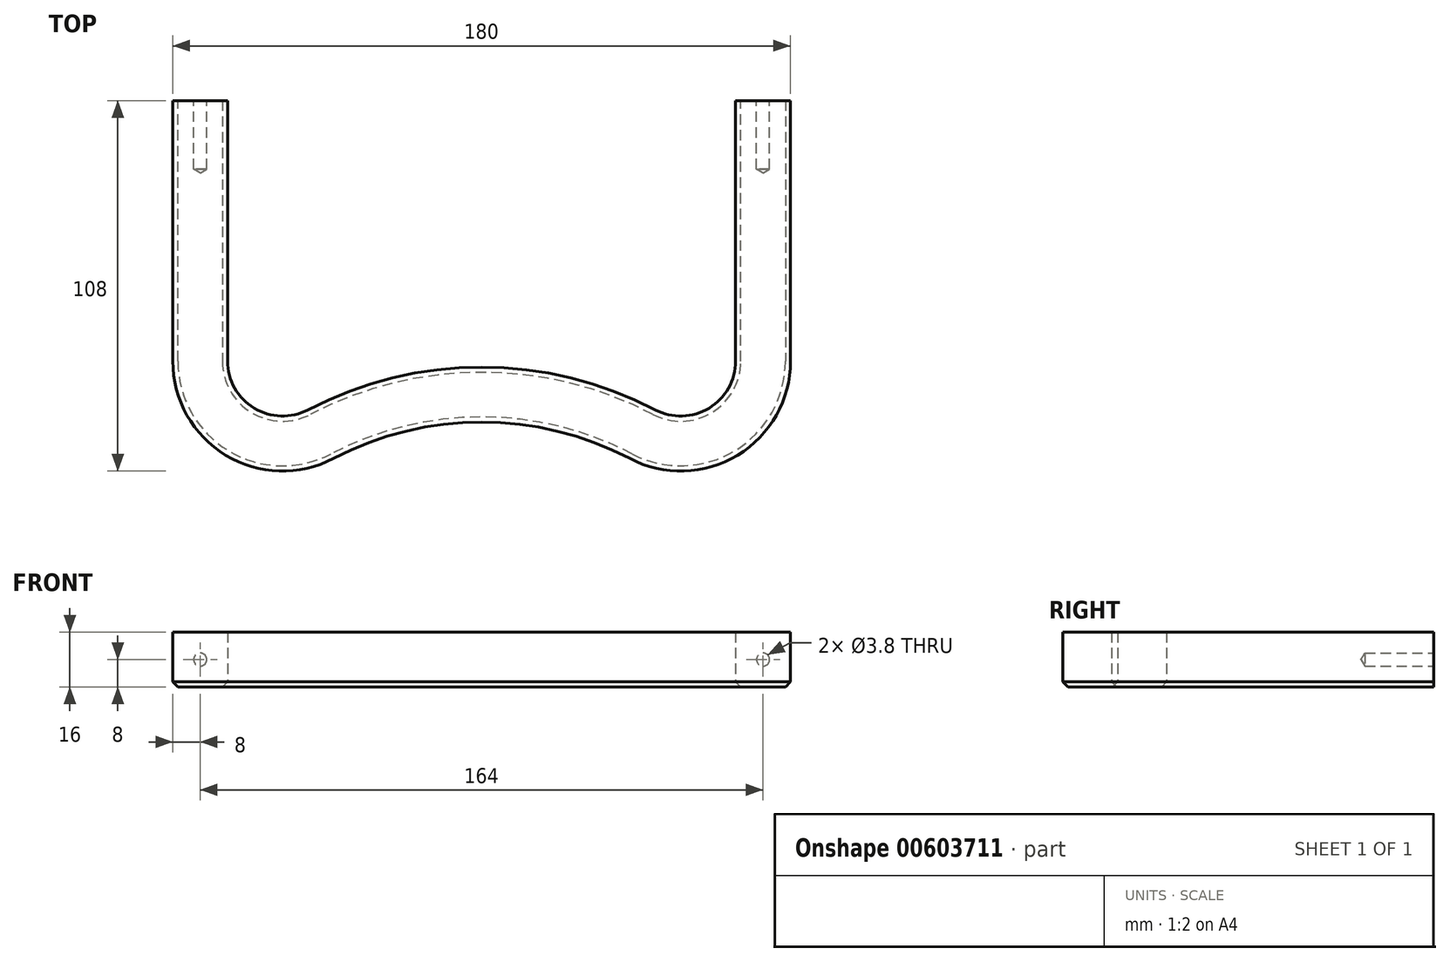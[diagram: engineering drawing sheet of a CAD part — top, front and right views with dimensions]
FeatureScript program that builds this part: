
annotation { "Feature Type Name" : "Feature", "Feature Type Description" : "" }
export const myFeature = defineFeature(function(context is Context, id is Id, definition is map)
    precondition{}
    {
        {
            var Q0;
            Q0=qCreatedBy(makeId("Top.planeOp"),FACE);
            var sketch = newSketch(context, id + "F0", { "sketchPlane" : qUnion([Q0])});
            skLineSegment(sketch, "E0", {"start": v(0, 84.42) * mm, "end": v(0, -84.76) * mm, "construction": true});
            skLineSegment(sketch, "E1.right", {"start": v(-74, 61.2) * mm, "end": v(-74, -14.8) * mm});
            skPoint(sketch, "E1.middle", {"position": v(0, 0) * mm});
            skArc(sketch, "E2", {"start": v(-74, -14.8) * mm, "mid": v(-66.29, -28.49) * mm, "end": v(-50.58, -28.98) * mm});
            skPoint(sketch, "E3.orphan", {"position": v(-74, -33.07) * mm});
            skArc(sketch, "E4", {"start": v(0, -16.55) * mm, "mid": v(-26.04, -19.7) * mm, "end": v(-50.58, -28.98) * mm});
            skArc(sketch, "E5.0", {"start": v(0, -32.55) * mm, "mid": v(-22.23, -35.24) * mm, "end": v(-43.17, -43.15) * mm});
            skArc(sketch, "E5.1", {"start": v(-90, -14.8) * mm, "mid": v(-74.57, -42.17) * mm, "end": v(-43.17, -43.15) * mm});
            skLineSegment(sketch, "E5.2", {"start": v(-90, 61.2) * mm, "end": v(-90, -14.8) * mm});
            skLineSegment(sketch, "E6", {"start": v(-90, 61.2) * mm, "end": v(-74, 61.2) * mm});
            skLineSegment(sketch, "E7.MirrorCS", {"start": v(90, 61.2) * mm, "end": v(74, 61.2) * mm});
            skLineSegment(sketch, "E8.MirrorCS", {"start": v(90, 61.2) * mm, "end": v(90, -14.8) * mm});
            skLineSegment(sketch, "E9.MirrorCS", {"start": v(74, 61.2) * mm, "end": v(74, -14.8) * mm});
            skArc(sketch, "E10.MirrorCS", {"start": v(90, -14.8) * mm, "mid": v(74.57, -42.17) * mm, "end": v(43.17, -43.15) * mm});
            skArc(sketch, "E11.MirrorCS", {"start": v(74, -14.8) * mm, "mid": v(66.29, -28.49) * mm, "end": v(50.58, -28.98) * mm});
            skArc(sketch, "E12.MirrorCS", {"start": v(0, -16.55) * mm, "mid": v(26.04, -19.7) * mm, "end": v(50.58, -28.98) * mm});
            skArc(sketch, "E13.MirrorCS", {"start": v(0, -32.55) * mm, "mid": v(22.23, -35.24) * mm, "end": v(43.17, -43.15) * mm});
            skSolve(sketch);
        }
        {
            var Q0;
            Q0=qSketchRegion(id+"F0",true);
            extrude(context, id + "F1", {"entities" : qUnion([Q0]), "depth" : 16 * mm, "offsetDistance" : 25 * mm});
        }
        {
            var Q0;
            Q0=makeQuery(id+"F1.opExtrude","SWEPT_FACE",FACE,{"disambiguationData":[OSD([sQuery(id+"F0.wireOp",EDGE,"E6")])]});
            var sketch = newSketch(context, id + "F2", { "sketchPlane" : qUnion([Q0])});
            skPoint(sketch, "E14", {"position": v(82, 8) * mm});
            skPoint(sketch, "E15", {"position": v(-82, 8) * mm});
            skSolve(sketch);
        }
        {
            var Q0;
            Q0=sQuery(id+"F2.wireOp",VERTEX,"E14");
            var Q1;
            Q1=sQuery(id+"F2.wireOp",VERTEX,"E15");
            var Q2;
            Q2=makeQuery(id+"F1.opExtrude","SWEPT_BODY",BODY,{"disambiguationData":[OSD([sQuery(id+"F0.wireOp",EDGE,"E1.right"),sQuery(id+"F0.wireOp",EDGE,"E2"),sQuery(id+"F0.wireOp",EDGE,"E4"),sQuery(id+"F0.wireOp",EDGE,"E5.0"),sQuery(id+"F0.wireOp",EDGE,"E5.1"),sQuery(id+"F0.wireOp",EDGE,"E5.2"),sQuery(id+"F0.wireOp",EDGE,"E6"),sQuery(id+"F0.wireOp",EDGE,"E7.MirrorCS"),sQuery(id+"F0.wireOp",EDGE,"E8.MirrorCS"),sQuery(id+"F0.wireOp",EDGE,"E9.MirrorCS"),sQuery(id+"F0.wireOp",EDGE,"E10.MirrorCS"),sQuery(id+"F0.wireOp",EDGE,"E11.MirrorCS"),sQuery(id+"F0.wireOp",EDGE,"E12.MirrorCS"),sQuery(id+"F0.wireOp",EDGE,"E13.MirrorCS")])]});
            hole(context, id + "F3", {"style" : HoleStyle.SIMPLE, "endStyle" : HoleEndStyle.BLIND, "holeDiameter" : 3.8 * mm, "majorDiameter" : 5 * mm, "holeDepth" : 20 * mm, "isTappedThrough" : true, "tappedDepth" : 12 * mm, "tapClearance" : 3, "startFromSketch" : true, "locations" : qUnion([Q0, Q1]), "scope" : qUnion([Q2])});
        }
        {
            var Q0;
            Q0=makeQuery(id+"F1.opExtrude","CAP_EDGE",EDGE,{"disambiguationData":[OSD([sQuery(id+"F0.wireOp",EDGE,"E10.MirrorCS")])],"isStart":true});
            var Q1;
            Q1=makeQuery(id+"F1.opExtrude","CAP_EDGE",EDGE,{"disambiguationData":[OSD([sQuery(id+"F0.wireOp",EDGE,"E11.MirrorCS")])],"isStart":true});
            chamfer(context, id + "F4", {"entities" : qUnion([Q0, Q1]), "width" : 1.5 * mm, "tangentPropagation" : true});
        }
    });
